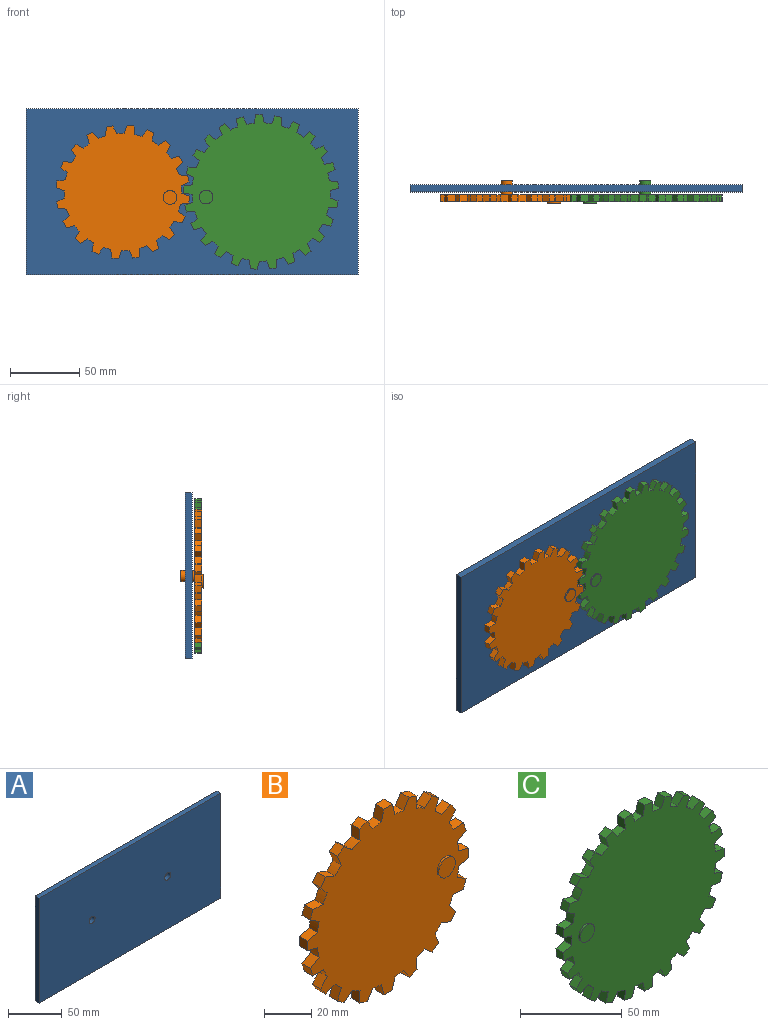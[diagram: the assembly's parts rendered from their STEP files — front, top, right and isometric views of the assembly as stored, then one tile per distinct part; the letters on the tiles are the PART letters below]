
ASSEMBLY  parts=3 mates=2
PART A: 8 faces, bbox 240x5x120 mm
  f0: plane 240x120mm, normal (0,-1,0), area 28699.5mm2, adj f2,f3,f4,f5,f6,f7
  f1: plane 240x120mm, normal (0,1,0), area 28699.5mm2, adj f2,f3,f4,f5,f6,f7
  f2: plane 240x5mm, normal (0,0,-1), area 1200mm2, adj f0,f1,f3,f5
  f3: plane 120x5mm, normal (1,0,0), area 600mm2, adj f0,f1,f2,f4
  f4: plane 240x5mm, normal (0,0,1), area 1200mm2, adj f0,f1,f3,f5
  f5: plane 120x5mm, normal (-1,0,0), area 600mm2, adj f0,f1,f2,f4
  f6: cylinder r=4mm len=8mm, axis (0,-1,0), area 125.7mm2, adj f0,f1
  f7: cylinder r=4mm len=8mm, axis (0,-1,0), area 125.7mm2, adj f0,f1
PART B: 86 faces, bbox 96.6x16x96.6 mm
  f0: cylinder r=42.5mm len=5mm, axis (0,1,0), area 26.7mm2, adj f25,f26,f74,f77
  f1: cylinder r=42.5mm len=5mm, axis (0,1,0), area 26.7mm2, adj f25,f26,f76,f80
  f2: cylinder r=42.5mm len=5mm, axis (0,1,0), area 26.7mm2, adj f25,f26,f79,f81
  f3: cylinder r=42.5mm len=5.27mm, axis (0,1,0), area 26.7mm2, adj f25,f26,f29,f82
  f4: cylinder r=42.5mm len=5.27mm, axis (0,1,0), area 26.7mm2, adj f25,f26,f28,f32
  f5: cylinder r=42.5mm len=5mm, axis (0,1,0), area 26.7mm2, adj f25,f26,f31,f35
  f6: cylinder r=42.5mm len=5mm, axis (0,1,0), area 26.7mm2, adj f25,f26,f34,f38
  f7: cylinder r=42.5mm len=5mm, axis (0,1,0), area 26.7mm2, adj f25,f26,f37,f41
  f8: cylinder r=42.5mm len=5.27mm, axis (0,1,0), area 26.7mm2, adj f25,f26,f40,f44
  f9: cylinder r=42.5mm len=5.27mm, axis (0,1,0), area 26.7mm2, adj f25,f26,f43,f47
  f10: cylinder r=42.5mm len=5mm, axis (0,1,0), area 26.7mm2, adj f25,f26,f46,f50
  f11: cylinder r=42.5mm len=5mm, axis (0,1,0), area 26.7mm2, adj f25,f26,f49,f53
  f12: cylinder r=42.5mm len=5mm, axis (0,1,0), area 26.7mm2, adj f25,f26,f52,f56
  f13: cylinder r=42.5mm len=5.27mm, axis (0,1,0), area 26.7mm2, adj f25,f26,f55,f59
  f14: cylinder r=42.5mm len=5.27mm, axis (0,1,0), area 26.7mm2, adj f25,f26,f58,f62
  f15: cylinder r=42.5mm len=5mm, axis (0,1,0), area 26.7mm2, adj f25,f26,f61,f65
  f16: cylinder r=42.5mm len=5mm, axis (0,1,0), area 26.7mm2, adj f25,f26,f64,f68
  f17: cylinder r=42.5mm len=5mm, axis (0,1,0), area 26.7mm2, adj f25,f26,f67,f71
  f18: cylinder r=42.5mm len=5.27mm, axis (0,1,0), area 26.7mm2, adj f21,f25,f26,f70
  f19: cylinder r=4mm len=10mm, axis (0,-1,0), area 251.3mm2, adj f20,f26
  f20: plane 8x8mm, normal (0,1,0), area 50.3mm2, adj f19
  f21: plane 6x5mm, normal (0.24,0,0.97), area 30.9mm2, adj f18,f24,f25,f26
  f22: cylinder r=42.5mm len=5.27mm, axis (0,1,0), area 26.7mm2, adj f23,f25,f26,f73
  f23: plane 6x5mm, normal (0.24,0,-0.97), area 30.9mm2, adj f22,f24,f25,f26
  f24: plane 5x5mm, normal (1,0,0), area 25mm2, adj f21,f23,f25,f26
  f25: plane 96.62x96.62mm, normal (0,-1,0), area 6355.8mm2, adj f0,f1,f2,f3,f4,f5,f6,f7
  f26: plane 96.62x96.62mm, normal (0,1,0), area 6384.1mm2, adj f0,f1,f2,f3,f4,f5,f6,f7
  f27: plane 5x5mm, normal (0,0,-1), area 25mm2, adj f25,f26,f28,f29
  f28: plane 6x5mm, normal (-0.97,0,-0.24), area 30.9mm2, adj f4,f25,f26,f27
  f29: plane 6x5mm, normal (0.97,0,-0.24), area 30.9mm2, adj f3,f25,f26,f27
  f30: plane 5x4.76mm, normal (-0.31,0,-0.95), area 25mm2, adj f25,f26,f31,f32
  f31: plane 6.17x5mm, normal (-1,0,0.07), area 30.9mm2, adj f5,f25,f26,f30
  f32: plane 5.24x5mm, normal (0.85,0,-0.53), area 30.9mm2, adj f4,f25,f26,f30
  f33: plane 5x4.05mm, normal (-0.59,0,-0.81), area 25mm2, adj f25,f26,f34,f35
  f34: plane 5.74x5mm, normal (-0.93,0,0.37), area 30.9mm2, adj f6,f25,f26,f33
  f35: plane 5x4.74mm, normal (0.64,0,-0.77), area 30.9mm2, adj f5,f25,f26,f33
  f36: plane 5x4.05mm, normal (-0.81,0,-0.59), area 25mm2, adj f25,f26,f37,f38
  f37: plane 5x4.74mm, normal (-0.77,0,0.64), area 30.9mm2, adj f7,f25,f26,f36
  f38: plane 5.74x5mm, normal (0.37,0,-0.93), area 30.9mm2, adj f6,f25,f26,f36
  f39: plane 5x4.76mm, normal (-0.95,0,-0.31), area 25mm2, adj f25,f26,f40,f41
  f40: plane 5.24x5mm, normal (-0.53,0,0.85), area 30.9mm2, adj f8,f25,f26,f39
  f41: plane 6.17x5mm, normal (0.07,0,-1), area 30.9mm2, adj f7,f25,f26,f39
  f42: plane 5x5mm, normal (-1,0,0), area 25mm2, adj f25,f26,f43,f44
  f43: plane 6x5mm, normal (-0.24,0,0.97), area 30.9mm2, adj f9,f25,f26,f42
  f44: plane 6x5mm, normal (-0.24,0,-0.97), area 30.9mm2, adj f8,f25,f26,f42
  f45: plane 5x4.76mm, normal (-0.95,0,0.31), area 25mm2, adj f25,f26,f46,f47
  f46: plane 6.17x5mm, normal (0.07,0,1), area 30.9mm2, adj f10,f25,f26,f45
  f47: plane 5.24x5mm, normal (-0.53,0,-0.85), area 30.9mm2, adj f9,f25,f26,f45
  f48: plane 5x4.05mm, normal (-0.81,0,0.59), area 25mm2, adj f25,f26,f49,f50
  f49: plane 5.74x5mm, normal (0.37,0,0.93), area 30.9mm2, adj f11,f25,f26,f48
  f50: plane 5x4.74mm, normal (-0.77,0,-0.64), area 30.9mm2, adj f10,f25,f26,f48
  f51: plane 5x4.05mm, normal (-0.59,0,0.81), area 25mm2, adj f25,f26,f52,f53
  f52: plane 5x4.74mm, normal (0.64,0,0.77), area 30.9mm2, adj f12,f25,f26,f51
  f53: plane 5.74x5mm, normal (-0.93,0,-0.37), area 30.9mm2, adj f11,f25,f26,f51
  f54: plane 5x4.76mm, normal (-0.31,0,0.95), area 25mm2, adj f25,f26,f55,f56
  f55: plane 5.24x5mm, normal (0.85,0,0.53), area 30.9mm2, adj f13,f25,f26,f54
  f56: plane 6.17x5mm, normal (-1,0,-0.07), area 30.9mm2, adj f12,f25,f26,f54
  f57: plane 5x5mm, normal (0,0,1), area 25mm2, adj f25,f26,f58,f59
  f58: plane 6x5mm, normal (0.97,0,0.24), area 30.9mm2, adj f14,f25,f26,f57
  f59: plane 6x5mm, normal (-0.97,0,0.24), area 30.9mm2, adj f13,f25,f26,f57
  f60: plane 5x4.76mm, normal (0.31,0,0.95), area 25mm2, adj f25,f26,f61,f62
  f61: plane 6.17x5mm, normal (1,0,-0.07), area 30.9mm2, adj f15,f25,f26,f60
  f62: plane 5.24x5mm, normal (-0.85,0,0.53), area 30.9mm2, adj f14,f25,f26,f60
  f63: plane 5x4.05mm, normal (0.59,0,0.81), area 25mm2, adj f25,f26,f64,f65
  f64: plane 5.74x5mm, normal (0.93,0,-0.37), area 30.9mm2, adj f16,f25,f26,f63
  f65: plane 5x4.74mm, normal (-0.64,0,0.77), area 30.9mm2, adj f15,f25,f26,f63
  f66: plane 5x4.05mm, normal (0.81,0,0.59), area 25mm2, adj f25,f26,f67,f68
  f67: plane 5x4.74mm, normal (0.77,0,-0.64), area 30.9mm2, adj f17,f25,f26,f66
  f68: plane 5.74x5mm, normal (-0.37,0,0.93), area 30.9mm2, adj f16,f25,f26,f66
  f69: plane 5x4.76mm, normal (0.95,0,0.31), area 25mm2, adj f25,f26,f70,f71
  f70: plane 5.24x5mm, normal (0.53,0,-0.85), area 30.9mm2, adj f18,f25,f26,f69
  f71: plane 6.17x5mm, normal (-0.07,0,1), area 30.9mm2, adj f17,f25,f26,f69
  f72: plane 5x4.76mm, normal (0.95,0,-0.31), area 25mm2, adj f25,f26,f73,f74
  f73: plane 5.24x5mm, normal (0.53,0,0.85), area 30.9mm2, adj f22,f25,f26,f72
  f74: plane 6.17x5mm, normal (-0.07,0,-1), area 30.9mm2, adj f0,f25,f26,f72
  f75: plane 5x4.05mm, normal (0.81,0,-0.59), area 25mm2, adj f25,f26,f76,f77
  f76: plane 5.74x5mm, normal (-0.37,0,-0.93), area 30.9mm2, adj f1,f25,f26,f75
  f77: plane 5x4.74mm, normal (0.77,0,0.64), area 30.9mm2, adj f0,f25,f26,f75
  f78: plane 5x4.05mm, normal (0.59,0,-0.81), area 25mm2, adj f25,f26,f79,f80
  f79: plane 5x4.74mm, normal (-0.64,0,-0.77), area 30.9mm2, adj f2,f25,f26,f78
  f80: plane 5.74x5mm, normal (0.93,0,0.37), area 30.9mm2, adj f1,f25,f26,f78
  f81: plane 6.17x5mm, normal (1,0,0.07), area 30.9mm2, adj f2,f25,f26,f83
  f82: plane 5.24x5mm, normal (-0.85,0,-0.53), area 30.9mm2, adj f3,f25,f26,f83
  f83: plane 5x4.76mm, normal (0.31,0,-0.95), area 25mm2, adj f25,f26,f81,f82
  f84: cylinder r=5mm len=10mm, axis (0,1,0), area 31.4mm2, adj f25,f85
  f85: plane 10x10mm, normal (0,-1,0), area 78.5mm2, adj f84
PART C: 106 faces, bbox 111.6x16x111.8 mm
  f0: cylinder r=4mm len=10mm, axis (0,-1,0), area 251.3mm2, adj f1,f103
  f1: plane 8x8mm, normal (0,1,0), area 50.3mm2, adj f0
  f2: plane 111.85x111.63mm, normal (0,-1,0), area 8661.1mm2, adj f3,f4,f5,f6,f7,f8,f9,f10
  f3: plane 6.02x5mm, normal (0.99,0,0.15), area 30.4mm2, adj f2,f4,f102,f103
  f4: cylinder r=50mm len=5.03mm, axis (0,1,0), area 27.8mm2, adj f2,f3,f5,f103
  f5: plane 5x4.53mm, normal (-0.74,0,-0.67), area 30.4mm2, adj f2,f4,f6,f103
  f6: plane 5x4.22mm, normal (0.54,0,-0.84), area 25mm2, adj f2,f5,f7,f103
  f7: plane 5.6x5mm, normal (0.92,0,0.39), area 30.4mm2, adj f2,f6,f8,f103
  f8: cylinder r=50mm len=5mm, axis (0,1,0), area 27.8mm2, adj f2,f7,f9,f103
  f9: plane 5.06x5mm, normal (-0.56,0,-0.83), area 30.4mm2, adj f2,f8,f10,f103
  f10: plane 5x3.65mm, normal (0.73,0,-0.68), area 25mm2, adj f2,f9,f11,f103
  f11: plane 5x4.84mm, normal (0.8,0,0.61), area 30.4mm2, adj f2,f10,f12,f103
  f12: cylinder r=50mm len=5mm, axis (0,1,0), area 27.8mm2, adj f2,f11,f13,f103
  f13: plane 5.74x5mm, normal (-0.33,0,-0.94), area 30.4mm2, adj f2,f12,f14,f103
  f14: plane 5x4.38mm, normal (0.88,0,-0.48), area 25mm2, adj f2,f13,f15,f103
  f15: plane 5x4.78mm, normal (0.62,0,0.79), area 30.4mm2, adj f2,f14,f16,f103
  f16: cylinder r=50mm len=5.17mm, axis (0,1,0), area 27.8mm2, adj f2,f15,f17,f103
  f17: plane 6.06x5mm, normal (-0.09,0,-1), area 30.4mm2, adj f2,f16,f18,f103
  f18: plane 5x4.84mm, normal (0.97,0,-0.25), area 25mm2, adj f2,f17,f19,f103
  f19: plane 5.56x5mm, normal (0.4,0,0.91), area 30.4mm2, adj f2,f18,f20,f103
  f20: cylinder r=50mm len=5.51mm, axis (0,1,0), area 27.8mm2, adj f2,f19,f21,f103
  f21: plane 6x5mm, normal (0.16,0,-0.99), area 30.4mm2, adj f2,f20,f22,f103
  f22: plane 5x5mm, normal (1,0,0), area 25mm2, adj f2,f21,f23,f103
  f23: plane 6x5mm, normal (0.16,0,0.99), area 30.4mm2, adj f2,f22,f24,f103
  f24: cylinder r=50mm len=5.51mm, axis (0,1,0), area 27.8mm2, adj f2,f23,f25,f103
  f25: plane 5.56x5mm, normal (0.4,0,-0.91), area 30.4mm2, adj f2,f24,f26,f103
  f26: plane 5x4.84mm, normal (0.97,0,0.25), area 25mm2, adj f2,f25,f27,f103
  f27: plane 6.06x5mm, normal (-0.09,0,1), area 30.4mm2, adj f2,f26,f28,f103
  f28: cylinder r=50mm len=5.17mm, axis (0,1,0), area 27.8mm2, adj f2,f27,f29,f103
  f29: plane 5x4.78mm, normal (0.62,0,-0.79), area 30.4mm2, adj f2,f28,f30,f103
  f30: plane 5x4.38mm, normal (0.88,0,0.48), area 25mm2, adj f2,f29,f31,f103
  f31: plane 5.74x5mm, normal (-0.33,0,0.94), area 30.4mm2, adj f2,f30,f32,f103
  f32: cylinder r=50mm len=5mm, axis (0,1,0), area 27.8mm2, adj f2,f31,f33,f103
  f33: plane 5x4.84mm, normal (0.8,0,-0.61), area 30.4mm2, adj f2,f32,f34,f103
  f34: plane 5x3.65mm, normal (0.73,0,0.68), area 25mm2, adj f2,f33,f35,f103
  f35: plane 5.06x5mm, normal (-0.56,0,0.83), area 30.4mm2, adj f2,f34,f36,f103
  f36: cylinder r=50mm len=5mm, axis (0,1,0), area 27.8mm2, adj f2,f35,f37,f103
  f37: plane 5.6x5mm, normal (0.92,0,-0.39), area 30.4mm2, adj f2,f36,f38,f103
  f38: plane 5x4.22mm, normal (0.54,0,0.84), area 25mm2, adj f2,f37,f39,f103
  f39: plane 5x4.53mm, normal (-0.74,0,0.67), area 30.4mm2, adj f2,f38,f40,f103
  f40: cylinder r=50mm len=5.03mm, axis (0,1,0), area 27.8mm2, adj f2,f39,f41,f103
  f41: plane 6.02x5mm, normal (0.99,0,-0.15), area 30.4mm2, adj f2,f40,f42,f103
  f42: plane 5x4.76mm, normal (0.31,0,0.95), area 25mm2, adj f2,f41,f43,f103
  f43: plane 5.4x5mm, normal (-0.89,0,0.46), area 30.4mm2, adj f2,f42,f44,f103
  f44: cylinder r=50mm len=5.46mm, axis (0,1,0), area 27.8mm2, adj f2,f43,f45,f103
  f45: plane 6.05x5mm, normal (0.99,0,0.1), area 30.4mm2, adj f2,f44,f46,f103
  f46: plane 5x4.99mm, normal (0.06,0,1), area 25mm2, adj f2,f45,f47,f103
  f47: plane 5.93x5mm, normal (-0.97,0,0.23), area 30.4mm2, adj f2,f46,f48,f103
  f48: cylinder r=50mm len=5.55mm, axis (0,1,0), area 27.8mm2, adj f2,f47,f49,f103
  f49: plane 5.71x5mm, normal (0.94,0,0.35), area 30.4mm2, adj f2,f48,f50,f103
  f50: plane 5x4.91mm, normal (-0.19,0,0.98), area 25mm2, adj f2,f49,f51,f103
  f51: plane 6.08x5mm, normal (-1,0,-0.02), area 30.4mm2, adj f2,f50,f52,f103
  f52: cylinder r=50mm len=5.29mm, axis (0,1,0), area 27.8mm2, adj f2,f51,f53,f103
  f53: plane 5x5mm, normal (0.82,0,0.57), area 30.4mm2, adj f2,f52,f54,f103
  f54: plane 5x4.52mm, normal (-0.43,0,0.9), area 25mm2, adj f2,f53,f55,f103
  f55: plane 5.85x5mm, normal (-0.96,0,-0.27), area 30.4mm2, adj f2,f54,f56,f103
  f56: cylinder r=50mm len=5mm, axis (0,1,0), area 27.8mm2, adj f2,f55,f57,f103
  f57: plane 5x4.6mm, normal (0.66,0,0.76), area 30.4mm2, adj f2,f56,f58,f103
  f58: plane 5x3.85mm, normal (-0.64,0,0.77), area 25mm2, adj f2,f57,f59,f103
  f59: plane 5.26x5mm, normal (-0.86,0,-0.5), area 30.4mm2, adj f2,f58,f60,f103
  f60: cylinder r=50mm len=5mm, axis (0,1,0), area 27.8mm2, adj f2,f59,f61,f103
  f61: plane 5.44x5mm, normal (0.45,0,0.89), area 30.4mm2, adj f2,f60,f62,f103
  f62: plane 5x4.05mm, normal (-0.81,0,0.59), area 25mm2, adj f2,f61,f63,f103
  f63: plane 5x4.34mm, normal (-0.71,0,-0.7), area 30.4mm2, adj f2,f62,f64,f103
  f64: cylinder r=50mm len=5mm, axis (0,1,0), area 27.8mm2, adj f2,f63,f65,f103
  f65: plane 5.95x5mm, normal (0.21,0,0.98), area 30.4mm2, adj f2,f64,f66,f103
  f66: plane 5x4.65mm, normal (-0.93,0,0.37), area 25mm2, adj f2,f65,f67,f103
  f67: plane 5.21x5mm, normal (-0.52,0,-0.86), area 30.4mm2, adj f2,f66,f68,f103
  f68: cylinder r=50mm len=5.38mm, axis (0,1,0), area 27.8mm2, adj f2,f67,f69,f103
  f69: plane 6.08x5mm, normal (-0.04,0,1), area 30.4mm2, adj f2,f68,f70,f103
  f70: plane 5x4.96mm, normal (-0.99,0,0.13), area 25mm2, adj f2,f69,f71,f103
  f71: plane 5.83x5mm, normal (-0.29,0,-0.96), area 30.4mm2, adj f2,f70,f72,f103
  f72: cylinder r=50mm len=5.56mm, axis (0,1,0), area 27.8mm2, adj f2,f71,f73,f103
  f73: plane 5.83x5mm, normal (-0.29,0,0.96), area 30.4mm2, adj f2,f72,f74,f103
  f74: plane 5x4.96mm, normal (-0.99,0,-0.13), area 25mm2, adj f2,f73,f75,f103
  f75: plane 6.08x5mm, normal (-0.04,0,-1), area 30.4mm2, adj f2,f74,f76,f103
  f76: cylinder r=50mm len=5.38mm, axis (0,1,0), area 27.8mm2, adj f2,f75,f77,f103
  f77: plane 5.21x5mm, normal (-0.52,0,0.86), area 30.4mm2, adj f2,f76,f78,f103
  f78: plane 5x4.65mm, normal (-0.93,0,-0.37), area 25mm2, adj f2,f77,f79,f103
  f79: plane 5.95x5mm, normal (0.21,0,-0.98), area 30.4mm2, adj f2,f78,f80,f103
  f80: cylinder r=50mm len=5mm, axis (0,1,0), area 27.8mm2, adj f2,f79,f81,f103
  f81: plane 5x4.34mm, normal (-0.71,0,0.7), area 30.4mm2, adj f2,f80,f82,f103
  f82: plane 5x4.05mm, normal (-0.81,0,-0.59), area 25mm2, adj f2,f81,f83,f103
  f83: plane 5.44x5mm, normal (0.45,0,-0.89), area 30.4mm2, adj f2,f82,f84,f103
  f84: cylinder r=50mm len=5mm, axis (0,1,0), area 27.8mm2, adj f2,f83,f85,f103
  f85: plane 5.26x5mm, normal (-0.86,0,0.5), area 30.4mm2, adj f2,f84,f86,f103
  f86: plane 5x3.85mm, normal (-0.64,0,-0.77), area 25mm2, adj f2,f85,f87,f103
  f87: plane 5x4.6mm, normal (0.66,0,-0.76), area 30.4mm2, adj f2,f86,f88,f103
  f88: cylinder r=50mm len=5mm, axis (0,1,0), area 27.8mm2, adj f2,f87,f89,f103
  f89: plane 5.85x5mm, normal (-0.96,0,0.27), area 30.4mm2, adj f2,f88,f90,f103
  f90: plane 5x4.52mm, normal (-0.43,0,-0.9), area 25mm2, adj f2,f89,f91,f103
  f91: plane 5x5mm, normal (0.82,0,-0.57), area 30.4mm2, adj f2,f90,f92,f103
  f92: cylinder r=50mm len=5.29mm, axis (0,1,0), area 27.8mm2, adj f2,f91,f93,f103
  f93: plane 6.08x5mm, normal (-1,0,0.02), area 30.4mm2, adj f2,f92,f94,f103
  f94: plane 5x4.91mm, normal (-0.19,0,-0.98), area 25mm2, adj f2,f93,f95,f103
  f95: plane 5.71x5mm, normal (0.94,0,-0.35), area 30.4mm2, adj f2,f94,f96,f103
  f96: cylinder r=50mm len=5.55mm, axis (0,1,0), area 27.8mm2, adj f2,f95,f97,f103
  f97: plane 5.93x5mm, normal (-0.97,0,-0.23), area 30.4mm2, adj f2,f96,f98,f103
  f98: plane 5x4.99mm, normal (0.06,0,-1), area 25mm2, adj f2,f97,f99,f103
  f99: plane 6.05x5mm, normal (0.99,0,-0.1), area 30.4mm2, adj f2,f98,f100,f103
  f100: cylinder r=50mm len=5.46mm, axis (0,1,0), area 27.8mm2, adj f2,f99,f101,f103
  f101: plane 5.4x5mm, normal (-0.89,0,-0.46), area 30.4mm2, adj f2,f100,f102,f103
  f102: plane 5x4.76mm, normal (0.31,0,-0.95), area 25mm2, adj f2,f3,f101,f103
  f103: plane 111.85x111.63mm, normal (0,1,0), area 8689.4mm2, adj f0,f3,f4,f5,f6,f7,f8,f9
  f104: cylinder r=5mm len=10mm, axis (0,1,0), area 31.4mm2, adj f2,f105
  f105: plane 10x10mm, normal (0,-1,0), area 78.5mm2, adj f104
PLACE A at identity fixed
PLACE B rot(axis=(0,1,0),6.5deg) t=(-0.33,-2,-5.69)mm
PLACE C rot(axis=(0,-1,0),5.2deg) t=(0.21,-2,-4.56)mm
MATE revolute A.f6 <-> C.f0  axis (0,-1,0) through (50,-5,0)mm
MATE revolute A.f7 <-> B.f19  axis (0,-1,0) through (-50,-5,0)mm
